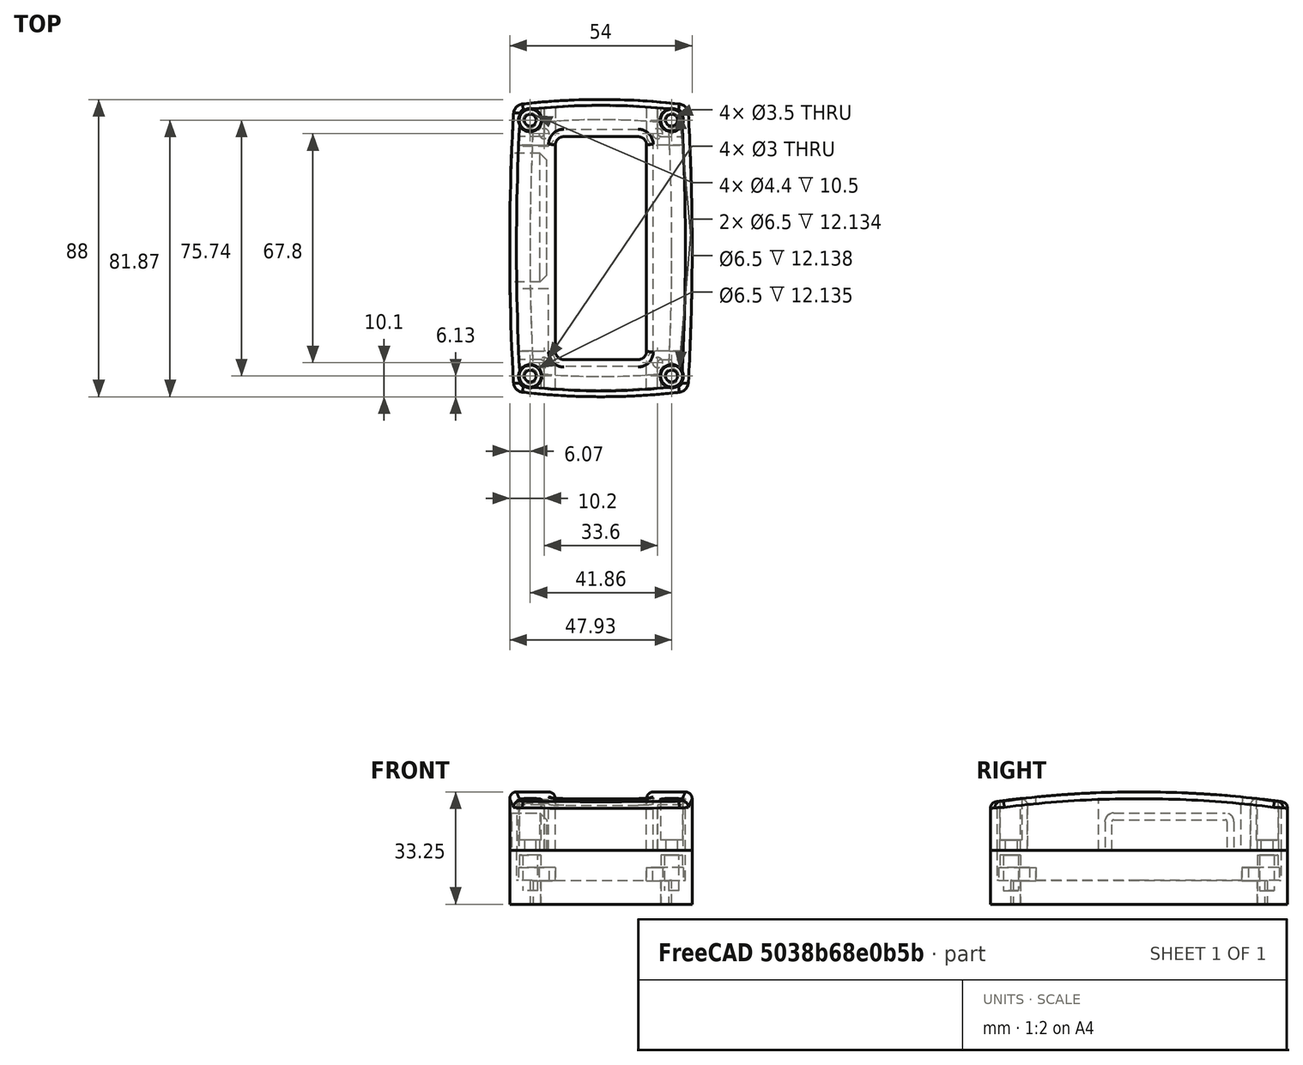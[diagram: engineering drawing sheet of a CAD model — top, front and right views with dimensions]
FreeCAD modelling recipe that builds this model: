
FCSTD DOCUMENT  (FreeCAD 0.20R29603 (Git))
Label: Cover
License: All rights reserved
LicenseURL: http://en.wikipedia.org/wiki/All_rights_reserved
objects: Part::Cylinder×42, Part::Box×21, Part::MultiFuse×21, Part::Fillet×20, Part::MultiCommon×13, Part::Cut×12, Part::Compound×12, Mesh::Feature×3, Part::Mirroring×3, Spreadsheet::Sheet×1, Part::Chamfer×1
note: 145 computed .brp shape members not serialized (recipe doc carries the construction recipe); baked Part::Feature solids carry a one-line shape summary decoded from their .brp

FEATURE [Mesh::Feature] Scouter_Cover
  Placement = pos=(-33.07,45.3,0) rot=(1,0,0;1.5708rad)
FEATURE [Part::Cylinder] Cylinder  label="Long Side circle"
  Angle = 360
  AttacherType = Attacher::AttachEngine3D
  FirstAngle = 0
  Height = 36
  Placement = pos=(673,0,0) rot=(0,0,1;0rad)
  Radius = 700
  SecondAngle = 0
  expr: .Placement.Base.x = Spreadsheet.B1 - 54 / 2
  expr: Radius = Spreadsheet.B1
FEATURE [Spreadsheet::Sheet] Spreadsheet
  cells = A1=long side; B1=700; A2=short side; B2=200; A3=top; B3=310; A4=center hole; B4=66; C4=27; D4=5; A5=Screw; B5=6.5; C5=3.5; A6=Screw head height; B6=3; A7=THreaded insert; B7=4.4
FEATURE [Part::Cylinder] Cylinder001  label="Short side circle"
  Angle = 360
  AttacherType = Attacher::AttachEngine3D
  FirstAngle = 0
  Height = 53
  Placement = pos=(0,156,0) rot=(0,0,1;0rad)
  Radius = 200
  SecondAngle = 0
  expr: .Placement.Base.y = Spreadsheet.B2 - 88 / 2
  expr: Radius = Spreadsheet.B2
FEATURE [Part::Cylinder] Cylinder002  label="Short side circle001"
  Angle = 360
  AttacherType = Attacher::AttachEngine3D
  FirstAngle = 0
  Height = 77
  Placement = pos=(-32,0,-278.75) rot=(0,1,0;1.5708rad)
  Radius = 310
  SecondAngle = 0
  expr: .Placement.Base.z = -(Spreadsheet.B3 - 31.25)
  expr: Radius = Spreadsheet.B3
FEATURE [Part::Box] Box  label="Cube"
  AttacherType = Attacher::AttachEngine3D
  Height = 29
  Length = 60
  Placement = pos=(-29.77,-50.31,14) rot=(0,0,1;0rad)
  Width = 99
FEATURE [Part::Cylinder] Cylinder003  label="Short side circle002"
  Angle = 360
  AttacherType = Attacher::AttachEngine3D
  FirstAngle = 0
  Height = 36
  Placement = pos=(0,-156,0) rot=(0,0,1;0rad)
  Radius = 200
  SecondAngle = 0
  expr: .Placement.Base.y = -(Spreadsheet.B2 - 88 / 2)
  expr: Radius = Spreadsheet.B2
FEATURE [Part::Cylinder] Cylinder004  label="Long Side circle001"
  Angle = 360
  AttacherType = Attacher::AttachEngine3D
  FirstAngle = 0
  Height = 36
  Placement = pos=(-673,0,0) rot=(0,0,1;0rad)
  Radius = 700
  SecondAngle = 0
  expr: .Placement.Base.x = -(Spreadsheet.B1 - 54 / 2)
  expr: Radius = Spreadsheet.B1
FEATURE [Part::MultiCommon] Common
  Shapes = -> [Box,Cylinder001]
FEATURE [Part::MultiCommon] Common001
  Shapes = -> [Cylinder002,Common]
FEATURE [Part::MultiCommon] Common002
  Shapes = -> [Cylinder,Common001]
FEATURE [Part::MultiCommon] Common003
  Shapes = -> [Cylinder004,Common002]
FEATURE [Part::MultiCommon] Common004
  Shapes = -> [Common003,Cylinder003]
FEATURE [Part::Box] Box001  label="Cube001"
  AttacherType = Attacher::AttachEngine3D
  Height = 54
  Length = 27
  Placement = pos=(-13.5,-33,0) rot=(0,0,1;0rad)
  Width = 66
  expr: .Placement.Base.x = -Spreadsheet.C4 / 2
  expr: .Placement.Base.y = -Spreadsheet.B4 / 2
  expr: Length = Spreadsheet.C4
  expr: Width = Spreadsheet.B4
FEATURE [Part::Fillet] Fillet  label="Centre hole"
  Base = -> Box001
  Edges = 4 edges r=2.5: [Edge1,Edge3,Edge5,Edge7]
FEATURE [Part::Cylinder] Cylinder005  label="Cylinder"
  Angle = 360
  AttacherType = Attacher::AttachEngine3D
  FirstAngle = 0
  Height = 20
  Placement = pos=(0,0,17) rot=(0,0,1;0rad)
  Radius = 3.25
  SecondAngle = 0
  expr: .Placement.Base.z = 14 + Spreadsheet.B6
  expr: Radius = Spreadsheet.B5 / 2
FEATURE [Part::Cylinder] Cylinder006
  Angle = 360
  AttacherType = Attacher::AttachEngine3D
  FirstAngle = 0
  Height = 39
  Radius = 1.75
  SecondAngle = 0
  expr: Radius = Spreadsheet.C5 / 2
FEATURE [Part::MultiFuse] Fusion  label="Screw hole"
  Placement = pos=(-20.93,37.87,0) rot=(0,0,1;0rad)
  Shapes = -> [Cylinder005,Cylinder006]
FEATURE [Part::Cut] Cut
  Base = -> Common004
  Tool = -> Fillet
FEATURE [Part::Fillet] Fillet001
  Base = -> Cut
  Edges = 17 edges: [Edge2 r=2,Edge3 r=3,Edge5 r=3,Edge6 r=2,Edge8 r=2,Edge9 r=2,Edge10 r=2,Edge11 r=2,Edge12 r=2,Edge13 r=2,Edge14 r=2,Edge15 r=2,Edge16 r=2,Edge17 r=2,Edge18 r=2,Edge19 r=3,Edge31 r=3]
FEATURE [Mesh::Feature] PCB
  Placement = pos=(-18.56,35.78,11.48) rot=(1,0,0;1.5708rad)
FEATURE [Part::Cylinder] Cylinder007
  Angle = 360
  AttacherType = Attacher::AttachEngine3D
  FirstAngle = 0
  Height = 20
  Placement = pos=(0,0,17) rot=(0,0,1;0rad)
  Radius = 3.25
  SecondAngle = 0
  expr: .Placement.Base.z = 14 + Spreadsheet.B6
  expr: Radius = Spreadsheet.B5 / 2
FEATURE [Part::Cylinder] Cylinder008
  Angle = 360
  AttacherType = Attacher::AttachEngine3D
  FirstAngle = 0
  Height = 39
  Radius = 1.75
  SecondAngle = 0
  expr: Radius = Spreadsheet.C5 / 2
FEATURE [Part::MultiFuse] Fusion001  label="Screw hole001"
  Placement = pos=(20.93,37.87,0) rot=(0,0,1;0rad)
  Shapes = -> [Cylinder007,Cylinder008]
FEATURE [Part::Cylinder] Cylinder009
  Angle = 360
  AttacherType = Attacher::AttachEngine3D
  FirstAngle = 0
  Height = 20
  Placement = pos=(0,0,17) rot=(0,0,1;0rad)
  Radius = 3.25
  SecondAngle = 0
  expr: .Placement.Base.z = 14 + Spreadsheet.B6
  expr: Radius = Spreadsheet.B5 / 2
FEATURE [Part::Cylinder] Cylinder010
  Angle = 360
  AttacherType = Attacher::AttachEngine3D
  FirstAngle = 0
  Height = 39
  Radius = 1.75
  SecondAngle = 0
  expr: Radius = Spreadsheet.C5 / 2
FEATURE [Part::MultiFuse] Fusion002  label="Screw hole002"
  Placement = pos=(-20.93,-37.87,0) rot=(0,0,1;0rad)
  Shapes = -> [Cylinder009,Cylinder010]
FEATURE [Part::Cylinder] Cylinder011
  Angle = 360
  AttacherType = Attacher::AttachEngine3D
  FirstAngle = 0
  Height = 20
  Placement = pos=(0,0,17) rot=(0,0,1;0rad)
  Radius = 3.25
  SecondAngle = 0
  expr: .Placement.Base.z = 14 + Spreadsheet.B6
  expr: Radius = Spreadsheet.B5 / 2
FEATURE [Part::Cylinder] Cylinder012
  Angle = 360
  AttacherType = Attacher::AttachEngine3D
  FirstAngle = 0
  Height = 39
  Radius = 1.75
  SecondAngle = 0
  expr: Radius = Spreadsheet.C5 / 2
FEATURE [Part::MultiFuse] Fusion003  label="Screw hole003"
  Placement = pos=(20.93,-37.87,0) rot=(0,0,1;0rad)
  Shapes = -> [Cylinder011,Cylinder012]
FEATURE [Part::MultiFuse] Fusion004  label="Screw holes"
  Shapes = -> [Fusion003,Fusion001,Fusion002,Fusion]
FEATURE [Part::Cut] Cut001
  Base = -> Fillet001
  Tool = -> Fusion004
FEATURE [Part::Box] Box002  label="Cube002"
  AttacherType = Attacher::AttachEngine3D
  Height = 12
  Length = 36
  Placement = pos=(-52,-10,13) rot=(0,0,1;0rad)
  Width = 38.08
FEATURE [Part::Fillet] Fillet002
  Base = -> Box002
  Edges = 2 edges r=2.5: [Edge10,Edge12]
FEATURE [Part::Chamfer] Chamfer
  Base = -> Fillet002
  Edges = 1 edges r=2: [Edge14]
FEATURE [Part::Cut] Cut002
  Base = -> Cut001
  Tool = -> Chamfer
FEATURE [Part::Box] Box003  label="Cube003"
  AttacherType = Attacher::AttachEngine3D
  Height = 29
  Length = 60
  Placement = pos=(-29.77,-50.31,14) rot=(0,0,1;0rad)
  Width = 99
FEATURE [Part::Cylinder] Cylinder013  label="Long Side circle002"
  Angle = 360
  AttacherType = Attacher::AttachEngine3D
  FirstAngle = 0
  Height = 36
  Placement = pos=(675,0,0) rot=(0,0,1;0rad)
  Radius = 700
  SecondAngle = 0
  expr: .Placement.Base.x = Spreadsheet.B1 - 54 / 2 + 2
  expr: Radius = Spreadsheet.B1
FEATURE [Part::Cylinder] Cylinder014  label="Short side circle003"
  Angle = 360
  AttacherType = Attacher::AttachEngine3D
  FirstAngle = 0
  Height = 53
  Placement = pos=(0,158,0) rot=(0,0,1;0rad)
  Radius = 200
  SecondAngle = 0
  expr: .Placement.Base.y = Spreadsheet.B2 - 88 / 2 + 2
  expr: Radius = Spreadsheet.B2
FEATURE [Part::MultiCommon] Common005
  Shapes = -> [Box003,Cylinder014]
FEATURE [Part::Cylinder] Cylinder015  label="Short side circle004"
  Angle = 360
  AttacherType = Attacher::AttachEngine3D
  FirstAngle = 0
  Height = 77
  Placement = pos=(-32,0,-280.75) rot=(0,1,0;1.5708rad)
  Radius = 310
  SecondAngle = 0
  expr: .Placement.Base.z = -(Spreadsheet.B3 - 31.25) - 2
  expr: Radius = Spreadsheet.B3
FEATURE [Part::MultiCommon] Common006
  Shapes = -> [Cylinder015,Common005]
FEATURE [Part::MultiCommon] Common007
  Shapes = -> [Cylinder013,Common006]
FEATURE [Part::Cylinder] Cylinder016  label="Short side circle005"
  Angle = 360
  AttacherType = Attacher::AttachEngine3D
  FirstAngle = 0
  Height = 36
  Placement = pos=(0,-158,0) rot=(0,0,1;0rad)
  Radius = 200
  SecondAngle = 0
  expr: .Placement.Base.y = -(Spreadsheet.B2 - 88 / 2) - 2
  expr: Radius = Spreadsheet.B2
FEATURE [Part::Cylinder] Cylinder017  label="Long Side circle003"
  Angle = 360
  AttacherType = Attacher::AttachEngine3D
  FirstAngle = 0
  Height = 36
  Placement = pos=(-675,0,0) rot=(0,0,1;0rad)
  Radius = 700
  SecondAngle = 0
  expr: .Placement.Base.x = -(Spreadsheet.B1 - 54 / 2) - 2
  expr: Radius = Spreadsheet.B1
FEATURE [Part::MultiCommon] Common008
  Shapes = -> [Cylinder017,Common007]
FEATURE [Part::MultiCommon] Common009  label="Full emptying"
  Placement = pos=(0,0,-0.05) rot=(0,0,1;0rad)
  Shapes = -> [Common008,Cylinder016]
FEATURE [Part::Box] Box004  label="Cube004"
  AttacherType = Attacher::AttachEngine3D
  Height = 75
  Length = 16
  Placement = pos=(-16.8,33,0) rot=(0,0,1;1.5708rad)
  Width = 11
FEATURE [Part::Fillet] Fillet003
  Base = -> Box004
  Edges = 1 edges r=1: [Edge1]
FEATURE [Part::Compound] Compound
  Links = -> [Fillet003]
FEATURE [Part::Box] Box005  label="Cube005"
  AttacherType = Attacher::AttachEngine3D
  Height = 75
  Length = 16
  Placement = pos=(-16.8,33,0) rot=(0,0,1;1.5708rad)
  Width = 11
FEATURE [Part::Fillet] Fillet004
  Base = -> Box005
  Edges = 1 edges r=1: [Edge1]
FEATURE [Part::Compound] Compound001
  Links = -> [Fillet004]
  Placement = pos=(0,0,0) rot=(0,0,1;-3.14159rad)
FEATURE [Part::MultiFuse] Fusion005
  Shapes = -> [Compound001,Compound]
FEATURE [Part::Box] Box006  label="Cube006"
  AttacherType = Attacher::AttachEngine3D
  Height = 75
  Length = 16
  Placement = pos=(-16.8,33,0) rot=(0,0,1;1.5708rad)
  Width = 11
FEATURE [Part::Box] Box007  label="Cube007"
  AttacherType = Attacher::AttachEngine3D
  Height = 75
  Length = 16
  Placement = pos=(-16.8,33,0) rot=(0,0,1;1.5708rad)
  Width = 11
FEATURE [Part::Fillet] Fillet005
  Base = -> Box006
  Edges = 1 edges r=1: [Edge1]
FEATURE [Part::Compound] Compound002
  Links = -> [Fillet005]
FEATURE [Part::Fillet] Fillet006
  Base = -> Box007
  Edges = 1 edges r=1: [Edge1]
FEATURE [Part::Compound] Compound003
  Links = -> [Fillet006]
  Placement = pos=(0,0,0) rot=(0,0,1;3.14159rad)
FEATURE [Part::MultiFuse] Fusion006
  Shapes = -> [Compound003,Compound002]
FEATURE [Part::Mirroring] Part__Mirroring  label="Fusion006 (Mirror #1)"
  Base = (0,0,0)
  Normal = (0,1,0)
  Source = -> Fusion006
FEATURE [Part::Box] Box008  label="Cube008"
  AttacherType = Attacher::AttachEngine3D
  Height = 20
  Length = 36
  Placement = pos=(-50,-12,13) rot=(0,0,1;0rad)
  Width = 42.08
FEATURE [Part::Box] Box009  label="Cube009"
  AttacherType = Attacher::AttachEngine3D
  Height = 54
  Length = 31
  Placement = pos=(-15.5,-35,0) rot=(0,0,1;0rad)
  Width = 70
  expr: .Placement.Base.x = -Spreadsheet.C4 / 2 - 2
  expr: .Placement.Base.y = -Spreadsheet.B4 / 2 - 2
  expr: Length = Spreadsheet.C4 + 4
  expr: Width = Spreadsheet.B4 + 4
FEATURE [Part::Fillet] Fillet007  label="Centre hole001"
  Base = -> Box009
  Edges = 4 edges r=4.5: [Edge1,Edge3,Edge5,Edge7]
FEATURE [Part::MultiFuse] Fusion007
  Shapes = -> [Fillet007,Part__Mirroring,Box008,Fusion005]
FEATURE [Part::Cut] Cut003
  Base = -> Common009
  Tool = -> Fusion007
FEATURE [Part::Cut] Cut004
  Base = -> Cut002
  Tool = -> Cut003
FEATURE [Part::Fillet] Fillet008  label="Cover"
  Base = -> Cut004
  Edges = 12 edges r=0.2: [Edge67,Edge68,Edge72,Edge73,Edge186,Edge187,Edge192,Edge193,Edge195,Edge196,Edge213,Edge214]
  Placement = pos=(0,0,3) rot=(0,0,1;0rad)
FEATURE [Part::Box] Box010  label="Cube010"
  AttacherType = Attacher::AttachEngine3D
  Height = 16
  Length = 60
  Placement = pos=(-29.77,-50.31,14) rot=(0,0,1;0rad)
  Width = 99
FEATURE [Part::Cylinder] Cylinder018  label="Long Side circle004"
  Angle = 360
  AttacherType = Attacher::AttachEngine3D
  FirstAngle = 0
  Height = 36
  Placement = pos=(673,0,0) rot=(0,0,1;0rad)
  Radius = 700
  SecondAngle = 0
  expr: .Placement.Base.x = Spreadsheet.B1 - 54 / 2
  expr: Radius = Spreadsheet.B1
FEATURE [Part::Cylinder] Cylinder019  label="Short side circle006"
  Angle = 360
  AttacherType = Attacher::AttachEngine3D
  FirstAngle = 0
  Height = 53
  Placement = pos=(0,156,0) rot=(0,0,1;0rad)
  Radius = 200
  SecondAngle = 0
  expr: .Placement.Base.y = Spreadsheet.B2 - 88 / 2
  expr: Radius = Spreadsheet.B2
FEATURE [Part::Cylinder] Cylinder021  label="Short side circle008"
  Angle = 360
  AttacherType = Attacher::AttachEngine3D
  FirstAngle = 0
  Height = 36
  Placement = pos=(0,-156,0) rot=(0,0,1;0rad)
  Radius = 200
  SecondAngle = 0
  expr: .Placement.Base.y = -(Spreadsheet.B2 - 88 / 2)
  expr: Radius = Spreadsheet.B2
FEATURE [Part::Cylinder] Cylinder022  label="Long Side circle005"
  Angle = 360
  AttacherType = Attacher::AttachEngine3D
  FirstAngle = 0
  Height = 36
  Placement = pos=(-673,0,0) rot=(0,0,1;0rad)
  Radius = 700
  SecondAngle = 0
  expr: .Placement.Base.x = -(Spreadsheet.B1 - 54 / 2)
  expr: Radius = Spreadsheet.B1
FEATURE [Part::MultiCommon] Common010  label="Body"
  Placement = pos=(0,0,-13) rot=(0,0,1;0rad)
  Shapes = -> [Box010,Cylinder018,Cylinder019,Cylinder021,Cylinder022]
FEATURE [Part::Box] Box011  label="Cube011"
  AttacherType = Attacher::AttachEngine3D
  Height = 16
  Length = 60
  Placement = pos=(-29.77,-50.31,11) rot=(0,0,1;0rad)
  Width = 99
FEATURE [Part::Cylinder] Cylinder023  label="Long Side circle006"
  Angle = 360
  AttacherType = Attacher::AttachEngine3D
  FirstAngle = 0
  Height = 36
  Placement = pos=(675,0,0) rot=(0,0,1;0rad)
  Radius = 700
  SecondAngle = 0
  expr: .Placement.Base.x = Spreadsheet.B1 - 54 / 2 + 2
  expr: Radius = Spreadsheet.B1
FEATURE [Part::Cylinder] Cylinder024  label="Short side circle009"
  Angle = 360
  AttacherType = Attacher::AttachEngine3D
  FirstAngle = 0
  Height = 53
  Placement = pos=(0,158,0) rot=(0,0,1;0rad)
  Radius = 200
  SecondAngle = 0
  expr: .Placement.Base.y = Spreadsheet.B2 - 88 / 2 + 2
  expr: Radius = Spreadsheet.B2
FEATURE [Part::Cylinder] Cylinder025  label="Short side circle010"
  Angle = 360
  AttacherType = Attacher::AttachEngine3D
  FirstAngle = 0
  Height = 36
  Placement = pos=(0,-158,0) rot=(0,0,1;0rad)
  Radius = 200
  SecondAngle = 0
  expr: .Placement.Base.y = -(Spreadsheet.B2 - 88 / 2) - 2
  expr: Radius = Spreadsheet.B2
FEATURE [Part::Cylinder] Cylinder026  label="Long Side circle007"
  Angle = 360
  AttacherType = Attacher::AttachEngine3D
  FirstAngle = 0
  Height = 36
  Placement = pos=(-675,0,0) rot=(0,0,1;0rad)
  Radius = 700
  SecondAngle = 0
  expr: .Placement.Base.x = -(Spreadsheet.B1 - 54 / 2) - 2
  expr: Radius = Spreadsheet.B1
FEATURE [Part::MultiCommon] Common011
  Placement = pos=(0,0,-3) rot=(0,0,1;0rad)
  Shapes = -> [Box011,Cylinder023,Cylinder024,Cylinder025,Cylinder026]
FEATURE [Part::Box] Box012  label="Cube012"
  AttacherType = Attacher::AttachEngine3D
  Height = 94
  Length = 60
  Placement = pos=(-29.77,-50.31,-4) rot=(0,0,1;0rad)
  Width = 99
FEATURE [Part::Cylinder] Cylinder027  label="Long Side circle008"
  Angle = 360
  AttacherType = Attacher::AttachEngine3D
  FirstAngle = 0
  Height = 36
  Placement = pos=(679,0,0) rot=(0,0,1;0rad)
  Radius = 700
  SecondAngle = 0
  expr: .Placement.Base.x = Spreadsheet.B1 - 54 / 2 + 6
  expr: Radius = Spreadsheet.B1
FEATURE [Part::Cylinder] Cylinder028  label="Short side circle011"
  Angle = 360
  AttacherType = Attacher::AttachEngine3D
  FirstAngle = 0
  Height = 53
  Placement = pos=(0,162,0) rot=(0,0,1;0rad)
  Radius = 200
  SecondAngle = 0
  expr: .Placement.Base.y = Spreadsheet.B2 - 88 / 2 + 6
  expr: Radius = Spreadsheet.B2
FEATURE [Part::Cylinder] Cylinder029  label="Short side circle012"
  Angle = 360
  AttacherType = Attacher::AttachEngine3D
  FirstAngle = 0
  Height = 36
  Placement = pos=(0,-162,0) rot=(0,0,1;0rad)
  Radius = 200
  SecondAngle = 0
  expr: .Placement.Base.y = -(Spreadsheet.B2 - 88 / 2) - 6
  expr: Radius = Spreadsheet.B2
FEATURE [Part::Cylinder] Cylinder030  label="Long Side circle009"
  Angle = 360
  AttacherType = Attacher::AttachEngine3D
  FirstAngle = 0
  Height = 36
  Placement = pos=(-679,0,0) rot=(0,0,1;0rad)
  Radius = 700
  SecondAngle = 0
  expr: .Placement.Base.x = -(Spreadsheet.B1 - 54 / 2) - 6
  expr: Radius = Spreadsheet.B1
FEATURE [Part::MultiCommon] Common012
  Placement = pos=(0,0,-13) rot=(0,0,1;0rad)
  Shapes = -> [Box012,Cylinder027,Cylinder028,Cylinder029,Cylinder030]
FEATURE [Part::Box] Box013  label="Cube013"
  AttacherType = Attacher::AttachEngine3D
  Height = 75
  Length = 16
  Placement = pos=(-17.8,35,0) rot=(0,0,1;1.5708rad)
  Width = 11
FEATURE [Part::Box] Box014  label="Cube014"
  AttacherType = Attacher::AttachEngine3D
  Height = 75
  Length = 16
  Placement = pos=(-17.8,35,0) rot=(0,0,1;1.5708rad)
  Width = 11
FEATURE [Part::Box] Box015  label="Cube015"
  AttacherType = Attacher::AttachEngine3D
  Height = 75
  Length = 16
  Placement = pos=(-17.8,35,0) rot=(0,0,1;1.5708rad)
  Width = 11
FEATURE [Part::Box] Box016  label="Cube016"
  AttacherType = Attacher::AttachEngine3D
  Height = 75
  Length = 16
  Placement = pos=(-17.8,35,0) rot=(0,0,1;1.5708rad)
  Width = 11
FEATURE [Part::Fillet] Fillet009
  Base = -> Box013
  Edges = 1 edges r=1: [Edge1]
FEATURE [Part::Compound] Compound004
  Links = -> [Fillet009]
FEATURE [Part::Fillet] Fillet010
  Base = -> Box014
  Edges = 1 edges r=1: [Edge1]
FEATURE [Part::Compound] Compound005
  Links = -> [Fillet010]
  Placement = pos=(0,0,0) rot=(0,0,1;3.14159rad)
FEATURE [Part::Fillet] Fillet011
  Base = -> Box015
  Edges = 1 edges r=1: [Edge1]
FEATURE [Part::Compound] Compound006
  Links = -> [Fillet011]
FEATURE [Part::Fillet] Fillet012
  Base = -> Box016
  Edges = 1 edges r=1: [Edge1]
FEATURE [Part::Compound] Compound007
  Links = -> [Fillet012]
  Placement = pos=(0,0,0) rot=(0,0,1;3.14159rad)
FEATURE [Part::MultiFuse] Fusion008
  Shapes = -> [Compound005,Compound004]
FEATURE [Part::MultiFuse] Fusion009
  Shapes = -> [Compound007,Compound006]
FEATURE [Part::Mirroring] Part__Mirroring001  label="Fusion006 (Mirror #1)001"
  Base = (0,0,0)
  Normal = (0,1,0)
  Source = -> Fusion009
FEATURE [Part::Fillet] Fillet013
  Base = -> Common011
  Edges = 4 edges r=3: [Edge7,Edge8,Edge12,Edge14]
FEATURE [Part::Fillet] Fillet014
  Base = -> Common012
  Edges = 4 edges r=3: [Edge7,Edge9,Edge12,Edge14]
FEATURE [Part::MultiFuse] Fusion010
  Shapes = -> [Fillet013,Fillet014]
FEATURE [Part::MultiFuse] Fusion011
  Placement = pos=(0,0,-59.5) rot=(0,0,1;0rad)
  Shapes = -> [Fusion008,Part__Mirroring001]
FEATURE [Part::Cut] Cut005
  Base = -> Fusion010
  Tool = -> Fusion011
FEATURE [Part::Cut] Cut006
  Base = -> Common010
  Tool = -> Cut005
FEATURE [Part::Cylinder] Cylinder031
  Angle = 360
  AttacherType = Attacher::AttachEngine3D
  FirstAngle = 0
  Height = 20
  Placement = pos=(0,0,17) rot=(0,0,1;0rad)
  Radius = 3.25
  SecondAngle = 0
  expr: .Placement.Base.z = 14 + Spreadsheet.B6
  expr: Radius = Spreadsheet.B5 / 2
FEATURE [Part::Cylinder] Cylinder032
  Angle = 360
  AttacherType = Attacher::AttachEngine3D
  FirstAngle = 0
  Height = 39
  Radius = 2.2
  SecondAngle = 0
  expr: Radius = Spreadsheet.B7 / 2
FEATURE [Part::Cylinder] Cylinder033
  Angle = 360
  AttacherType = Attacher::AttachEngine3D
  FirstAngle = 0
  Height = 20
  Placement = pos=(0,0,17) rot=(0,0,1;0rad)
  Radius = 3.25
  SecondAngle = 0
  expr: .Placement.Base.z = 14 + Spreadsheet.B6
  expr: Radius = Spreadsheet.B5 / 2
FEATURE [Part::Cylinder] Cylinder034
  Angle = 360
  AttacherType = Attacher::AttachEngine3D
  FirstAngle = 0
  Height = 39
  Radius = 2.2
  SecondAngle = 0
  expr: Radius = Spreadsheet.B7 / 2
FEATURE [Part::Cylinder] Cylinder035
  Angle = 360
  AttacherType = Attacher::AttachEngine3D
  FirstAngle = 0
  Height = 20
  Placement = pos=(0,0,17) rot=(0,0,1;0rad)
  Radius = 3.25
  SecondAngle = 0
  expr: .Placement.Base.z = 14 + Spreadsheet.B6
  expr: Radius = Spreadsheet.B5 / 2
FEATURE [Part::Cylinder] Cylinder036
  Angle = 360
  AttacherType = Attacher::AttachEngine3D
  FirstAngle = 0
  Height = 39
  Radius = 2.2
  SecondAngle = 0
  expr: Radius = Spreadsheet.B7 / 2
FEATURE [Part::Cylinder] Cylinder037
  Angle = 360
  AttacherType = Attacher::AttachEngine3D
  FirstAngle = 0
  Height = 20
  Placement = pos=(0,0,17) rot=(0,0,1;0rad)
  Radius = 3.25
  SecondAngle = 0
  expr: .Placement.Base.z = 14 + Spreadsheet.B6
  expr: Radius = Spreadsheet.B5 / 2
FEATURE [Part::Cylinder] Cylinder038
  Angle = 360
  AttacherType = Attacher::AttachEngine3D
  FirstAngle = 0
  Height = 39
  Radius = 2.2
  SecondAngle = 0
  expr: Radius = Spreadsheet.B7 / 2
FEATURE [Part::MultiFuse] Fusion012  label="Screw hole004"
  Placement = pos=(-20.93,37.87,0) rot=(0,0,1;0rad)
  Shapes = -> [Cylinder031,Cylinder032]
FEATURE [Part::MultiFuse] Fusion013  label="Screw hole005"
  Placement = pos=(20.93,37.87,0) rot=(0,0,1;0rad)
  Shapes = -> [Cylinder033,Cylinder034]
FEATURE [Part::MultiFuse] Fusion014  label="Screw hole006"
  Placement = pos=(-20.93,-37.87,0) rot=(0,0,1;0rad)
  Shapes = -> [Cylinder035,Cylinder036]
FEATURE [Part::MultiFuse] Fusion015  label="Screw hole007"
  Placement = pos=(20.93,-37.87,0) rot=(0,0,1;0rad)
  Shapes = -> [Cylinder037,Cylinder038]
FEATURE [Part::MultiFuse] Fusion016  label="Screw holes001"
  Placement = pos=(0,0,5) rot=(0,0,1;0rad)
  Shapes = -> [Fusion015,Fusion013,Fusion014,Fusion012]
FEATURE [Mesh::Feature] Scouter_Body001
  Placement = pos=(-26.91,44.05,0.61) rot=(1,0,0;1.5708rad)
FEATURE [Part::Box] Box017  label="Cube017"
  AttacherType = Attacher::AttachEngine3D
  Height = 4
  Length = 11.5
  Placement = pos=(-25,-42,7.9) rot=(0,0,1;0rad)
  Width = 11.5
FEATURE [Part::Fillet] Fillet016
  Base = -> Box017
  Edges = 2 edges r=3: [Edge1,Edge7]
FEATURE [Part::Cylinder] Cylinder039
  Angle = 360
  AttacherType = Attacher::AttachEngine3D
  FirstAngle = 0
  Height = 10
  Placement = pos=(-16.8,-33.9,7) rot=(0,0,1;0rad)
  Radius = 1.5
  SecondAngle = 0
FEATURE [Part::Cut] Cut008
  Base = -> Fillet016
  Tool = -> Cylinder039
FEATURE [Part::Compound] Compound008
  Links = -> [Cut008]
FEATURE [Part::Box] Box018  label="Cube018"
  AttacherType = Attacher::AttachEngine3D
  Height = 4
  Length = 11.5
  Placement = pos=(-25,-42,7.9) rot=(0,0,1;0rad)
  Width = 11.5
FEATURE [Part::Cylinder] Cylinder040
  Angle = 360
  AttacherType = Attacher::AttachEngine3D
  FirstAngle = 0
  Height = 10
  Placement = pos=(-16.8,-33.9,7) rot=(0,0,1;0rad)
  Radius = 1.5
  SecondAngle = 0
FEATURE [Part::Fillet] Fillet017
  Base = -> Box018
  Edges = 2 edges r=3: [Edge1,Edge7]
FEATURE [Part::Cut] Cut009
  Base = -> Fillet017
  Tool = -> Cylinder040
FEATURE [Part::Compound] Compound009
  Links = -> [Cut009]
  Placement = pos=(0,0,0) rot=(0,0,1;3.14159rad)
FEATURE [Part::MultiFuse] Fusion017
  Shapes = -> [Compound009,Compound008]
FEATURE [Part::Mirroring] Part__Mirroring002  label="Fusion017 (Mirror #3)"
  Base = (0,0,0)
  Normal = (0,1,0)
  Source = -> Fusion017
FEATURE [Part::Box] Box019  label="Cube019"
  AttacherType = Attacher::AttachEngine3D
  Height = 4
  Length = 11.5
  Placement = pos=(-25,-42,7.9) rot=(0,0,1;0rad)
  Width = 11.5
FEATURE [Part::Box] Box020  label="Cube020"
  AttacherType = Attacher::AttachEngine3D
  Height = 4
  Length = 11.5
  Placement = pos=(-25,-42,7.9) rot=(0,0,1;0rad)
  Width = 11.5
FEATURE [Part::Cylinder] Cylinder041
  Angle = 360
  AttacherType = Attacher::AttachEngine3D
  FirstAngle = 0
  Height = 10
  Placement = pos=(-16.8,-33.9,7) rot=(0,0,1;0rad)
  Radius = 1.5
  SecondAngle = 0
FEATURE [Part::Cylinder] Cylinder042
  Angle = 360
  AttacherType = Attacher::AttachEngine3D
  FirstAngle = 0
  Height = 10
  Placement = pos=(-16.8,-33.9,7) rot=(0,0,1;0rad)
  Radius = 1.5
  SecondAngle = 0
FEATURE [Part::Fillet] Fillet018
  Base = -> Box019
  Edges = 2 edges r=3: [Edge1,Edge7]
FEATURE [Part::Cut] Cut010
  Base = -> Fillet018
  Tool = -> Cylinder041
FEATURE [Part::Compound] Compound010
  Links = -> [Cut010]
FEATURE [Part::Fillet] Fillet019
  Base = -> Box020
  Edges = 2 edges r=3: [Edge1,Edge7]
FEATURE [Part::Cut] Cut011
  Base = -> Fillet019
  Tool = -> Cylinder042
FEATURE [Part::Compound] Compound011
  Links = -> [Cut011]
  Placement = pos=(0,0,0) rot=(0,0,1;3.14159rad)
FEATURE [Part::MultiFuse] Fusion018
  Shapes = -> [Compound011,Compound010]
FEATURE [Part::MultiFuse] Fusion019  label="inner screwtabs"
  Shapes = -> [Fusion018,Part__Mirroring002]
FEATURE [Part::MultiFuse] Fusion020
  Shapes = -> [Cut006,Fusion019]
FEATURE [Part::Cut] Cut012
  Base = -> Fusion020
  Tool = -> Fusion016
FEATURE [Part::Fillet] Fillet020
  Base = -> Cut012
  Edges = 4 edges r=3: [Edge32,Edge33,Edge35,Edge39]
